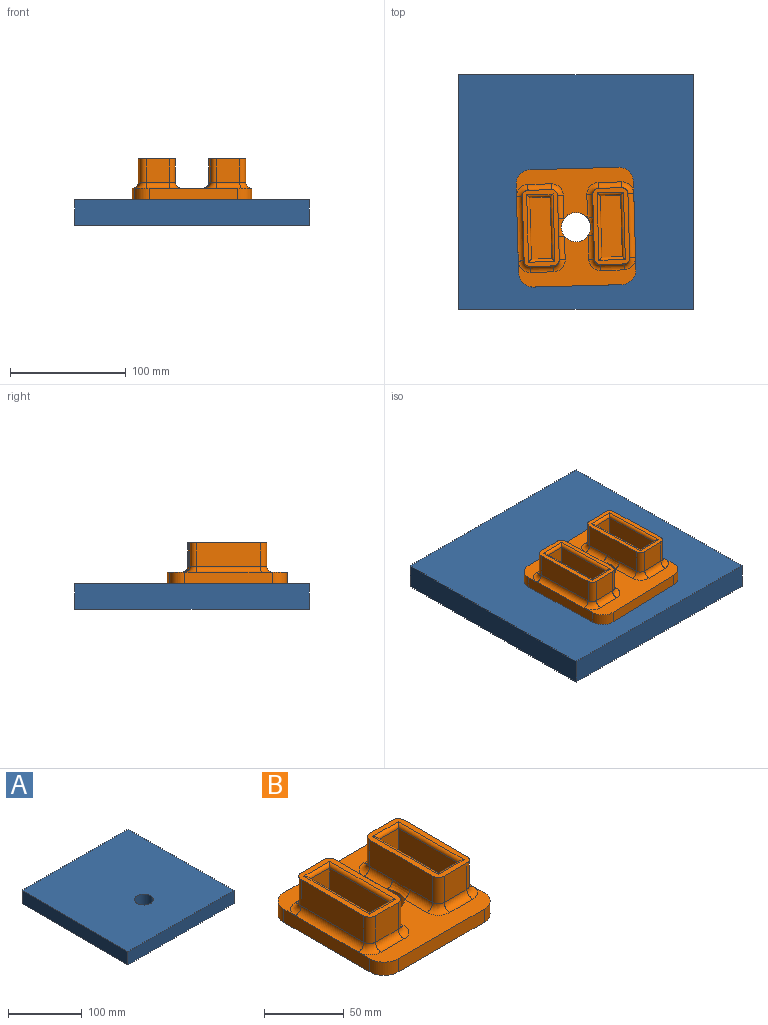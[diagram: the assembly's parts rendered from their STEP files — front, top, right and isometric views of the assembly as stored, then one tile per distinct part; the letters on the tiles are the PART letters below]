
ASSEMBLY  parts=2 mates=1
PART A: 7 faces, bbox 203.2x203.2x21.8 mm
  f0: plane 203.2x21.84mm, normal (0,-1,0), area 4438.7mm2, adj f1,f4,f5,f6
  f1: plane 203.2x21.84mm, normal (1,0,0), area 4438.7mm2, adj f0,f2,f5,f6
  f2: plane 203.2x21.84mm, normal (0,1,0), area 4438.7mm2, adj f1,f4,f5,f6
  f3: cylinder r=12.7mm len=25.4mm, axis (0,0,-1), area 1743.1mm2, adj f5,f6
  f4: plane 203.2x21.84mm, normal (-1,0,0), area 4438.7mm2, adj f0,f2,f5,f6
  f5: plane 203.2x203.2mm, normal (0,0,1), area 40783.5mm2, adj f0,f1,f2,f3,f4
  f6: plane 203.2x203.2mm, normal (0,0,-1), area 40783.5mm2, adj f0,f1,f2,f3,f4
PART B: 68 faces, bbox 111.1x101.6x35.6 mm
  f0: plane 101.6x43.18mm, normal (0,0,1), area 1856.9mm2, adj f2,f4,f5,f6,f30,f31,f48,f50
  f1: plane 101.6x43.18mm, normal (0,0,1), area 1856.9mm2, adj f2,f3,f4,f5,f28,f29,f41,f43
  f2: plane 76.2x10.16mm, normal (1,0,0), area 774.2mm2, adj f0,f1,f7,f28,f31,f46
  f3: plane 76.2x10.16mm, normal (0,1,0), area 774.2mm2, adj f1,f7,f28,f29
  f4: plane 76.2x10.16mm, normal (-1,0,0), area 774.2mm2, adj f0,f1,f7,f29,f30,f60
  f5: cylinder r=12.7mm len=25.4mm, axis (0,0,-1), area 810.7mm2, adj f0,f1,f7,f49,f62
  f6: plane 76.2x10.16mm, normal (0,-1,0), area 774.2mm2, adj f0,f7,f30,f31
  f7: plane 101.6x101.6mm, normal (0,0,-1), area 9677.4mm2, adj f2,f3,f4,f5,f6,f28,f29,f30
  f8: plane 55.88x21mm, normal (1,0,0), area 1140.7mm2, adj f16,f54,f59,f62,f64,f67
  f9: plane 20.32x20.32mm, normal (0,1,0), area 412.9mm2, adj f16,f54,f55,f56
  f10: plane 55.88x20.32mm, normal (-1,0,0), area 1135.5mm2, adj f16,f56,f60,f61
  f11: plane 53.34x22.86mm, normal (-1,0,0), area 1219.4mm2, adj f12,f14,f17,f37
  f12: plane 22.86x17.78mm, normal (0,1,0), area 406.5mm2, adj f11,f13,f17,f39
  f13: plane 53.34x22.86mm, normal (1,0,0), area 1219.4mm2, adj f12,f14,f17,f38
  f14: plane 22.86x17.78mm, normal (0,-1,0), area 406.5mm2, adj f11,f13,f17,f36
  f15: plane 20.32x20.32mm, normal (0,-1,0), area 412.9mm2, adj f16,f61,f65,f67
  f16: plane 66.04x30.48mm, normal (0,0,1), area 655.3mm2, adj f8,f9,f10,f15,f36,f37,f38,f39
  f17: plane 53.34x17.78mm, normal (0,0,1), area 948.4mm2, adj f11,f12,f13,f14
  f18: plane 55.88x21mm, normal (-1,0,0), area 1140.7mm2, adj f26,f42,f47,f49,f51,f53
  f19: plane 20.32x20.32mm, normal (0,-1,0), area 412.9mm2, adj f26,f45,f50,f53
  f20: plane 55.88x20.32mm, normal (1,0,0), area 1135.5mm2, adj f26,f40,f45,f46
  f21: plane 53.34x22.86mm, normal (1,0,0), area 1219.4mm2, adj f22,f24,f27,f33
  f22: plane 22.86x17.78mm, normal (0,-1,0), area 406.5mm2, adj f21,f23,f27,f32
  f23: plane 53.34x22.86mm, normal (-1,0,0), area 1219.4mm2, adj f22,f24,f27,f34
  f24: plane 22.86x17.78mm, normal (0,1,0), area 406.5mm2, adj f21,f23,f27,f35
  f25: plane 20.32x20.32mm, normal (0,1,0), area 412.9mm2, adj f26,f40,f41,f42
  f26: plane 66.04x30.48mm, normal (0,0,1), area 655.3mm2, adj f18,f19,f20,f25,f32,f33,f34,f35
  f27: plane 53.34x17.78mm, normal (0,0,1), area 948.4mm2, adj f21,f22,f23,f24
  f28: cylinder r=12.7mm len=12.7mm, axis (0,0,-1), area 202.7mm2, adj f1,f2,f3,f7
  f29: cylinder r=12.7mm len=12.7mm, axis (0,0,1), area 202.7mm2, adj f1,f3,f4,f7
  f30: cylinder r=12.7mm len=12.7mm, axis (0,0,-1), area 202.7mm2, adj f0,f4,f6,f7
  f31: cylinder r=12.7mm len=12.7mm, axis (0,0,1), area 202.7mm2, adj f0,f2,f6,f7
  f32: cylinder r=2.54mm len=22.86mm, axis (-1,0,0), area 81.1mm2, adj f22,f26,f33,f34
  f33: cylinder r=2.54mm len=58.42mm, axis (0,-1,0), area 223mm2, adj f21,f26,f32,f35
  f34: cylinder r=2.54mm len=58.42mm, axis (0,1,0), area 223mm2, adj f23,f26,f32,f35
  f35: cylinder r=2.54mm len=22.86mm, axis (1,0,0), area 81.1mm2, adj f24,f26,f33,f34
  f36: cylinder r=2.54mm len=22.86mm, axis (-1,0,0), area 81.1mm2, adj f14,f16,f37,f38
  f37: cylinder r=2.54mm len=58.42mm, axis (0,1,0), area 223mm2, adj f11,f16,f36,f39
  f38: cylinder r=2.54mm len=58.42mm, axis (0,-1,0), area 223mm2, adj f13,f16,f36,f39
  f39: cylinder r=2.54mm len=22.86mm, axis (1,0,0), area 81.1mm2, adj f12,f16,f37,f38
  f40: cylinder r=5.08mm len=20.32mm, axis (0,0,1), area 162.1mm2, adj f20,f25,f26,f43
  f41: cylinder r=5.08mm len=20.32mm, axis (-1,0,0), area 162.1mm2, adj f1,f25,f43,f44
  f42: cylinder r=5.08mm len=20.32mm, axis (0,0,-1), area 162.1mm2, adj f18,f25,f26,f44
  f43: torus R=10.16mm, axis (0,0,1), area 86.8mm2, adj f1,f40,f41,f46
  f44: torus R=10.16mm, axis (0,0,1), area 86.8mm2, adj f1,f41,f42,f47
  f45: cylinder r=5.08mm len=20.32mm, axis (0,0,-1), area 162.1mm2, adj f19,f20,f26,f48
  f46: cylinder r=5.08mm len=55.88mm, axis (0,1,0), area 445.9mm2, adj f2,f20,f43,f48
  f47: cylinder r=5.08mm len=20.32mm, axis (0,-1,0), area 162.1mm2, adj f1,f18,f44,f49
  f48: torus R=10.16mm, axis (0,0,1), area 86.8mm2, adj f0,f45,f46,f50
  f49: bspline ~15.24x5.08mm, area 94.8mm2, adj f5,f18,f47,f51
  f50: cylinder r=5.08mm len=20.32mm, axis (1,0,0), area 162.1mm2, adj f0,f19,f48,f52
  f51: cylinder r=5.08mm len=20.32mm, axis (0,-1,0), area 162.1mm2, adj f0,f18,f49,f52
  f52: torus R=10.16mm, axis (0,0,1), area 86.8mm2, adj f0,f50,f51,f53
  f53: cylinder r=5.08mm len=20.32mm, axis (0,0,1), area 162.1mm2, adj f18,f19,f26,f52
  f54: cylinder r=5.08mm len=20.32mm, axis (0,0,-1), area 162.1mm2, adj f8,f9,f16,f57
  f55: cylinder r=5.08mm len=20.32mm, axis (-1,0,0), area 162.1mm2, adj f1,f9,f57,f58
  f56: cylinder r=5.08mm len=20.32mm, axis (0,0,1), area 162.1mm2, adj f9,f10,f16,f58
  f57: torus R=10.16mm, axis (0,0,1), area 86.8mm2, adj f1,f54,f55,f59
  f58: torus R=10.16mm, axis (0,0,1), area 86.8mm2, adj f1,f55,f56,f60
  f59: cylinder r=5.08mm len=20.32mm, axis (0,1,0), area 162.1mm2, adj f1,f8,f57,f62
  f60: cylinder r=5.08mm len=55.88mm, axis (0,-1,0), area 445.9mm2, adj f4,f10,f58,f63
  f61: cylinder r=5.08mm len=20.32mm, axis (0,0,-1), area 162.1mm2, adj f10,f15,f16,f63
  f62: bspline ~15.24x5.08mm, area 94.8mm2, adj f5,f8,f59,f64
  f63: torus R=10.16mm, axis (0,0,1), area 86.8mm2, adj f0,f60,f61,f65
  f64: cylinder r=5.08mm len=20.32mm, axis (0,1,0), area 162.1mm2, adj f0,f8,f62,f66
  f65: cylinder r=5.08mm len=20.32mm, axis (1,0,0), area 162.1mm2, adj f0,f15,f63,f66
  f66: torus R=10.16mm, axis (0,0,1), area 86.8mm2, adj f0,f64,f65,f67
  f67: cylinder r=5.08mm len=20.32mm, axis (0,0,1), area 162.1mm2, adj f8,f15,f16,f66
PLACE A at identity fixed
PLACE B rot(axis=(0,0,1),1.6deg) t=(0,-30.48,21.84)mm
MATE revolute B.f5 <-> A.f3  axis (0,0,-1) through (0,-30.48,21.84)mm
